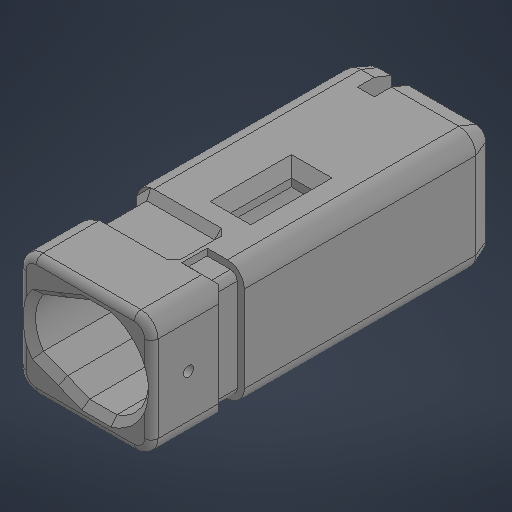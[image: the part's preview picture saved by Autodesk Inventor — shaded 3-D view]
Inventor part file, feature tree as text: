
AUTODESK INVENTOR PART (.ipt)
format: ipt  version: 2025.1 (Build 291241000, 241)  size: 1,372,672 bytes
history: native  units: in
note: dims shown in document units (in); Inventor stores cm internally (conversion verified against a paired STEP export)
features: extrude x9, sketch x8, chamfer x7, fillet x5, plane x1, projected_geometry x1
ambient origin geometry x8: Origin, YZ Plane, XZ Plane, XY Plane, X Axis, Y Axis, Z Axis, Center Point
bodies: Solid1 (feature_tree)
feature tree (31):
  extrude  "Extrusion1"  Depth=1.5354in
  extrude  "Extrusion2"  Depth=0.6988in
  chamfer  "Chamfer9"  Distance=3.9724in
  extrude  "Extrusion3"  Depth=3.9724in
  sketch  "Sketch5"  dims[d11=1.315in d12=1.0039in d13=0.5748in d14=0.2795in d15=0.2581in d16=0.1063in d17=0.5259in d18=0.4908in d30=3.9724in d31=-0.0019in]
  extrude  "Extrusion5"  Depth=0.0394in
  extrude  "Extrusion11"  TaperAngle=0.0deg  [1 undecoded]
  sketch  "Sketch9"  dims[d33=0.0394in d39=0.0394in]
  plane  "Work Plane1"
  extrude  "Extrusion9"  Depth=0.0394in
  chamfer  "Chamfer15"  Distance=0.7874in
  fillet  "Fillet3"  Radius=0.2953in
  chamfer  "Chamfer6"  Distance=0.0827in
  chamfer  "Chamfer11"  Distance=0.0787in
  fillet  "Fillet8"  Radius=0.2756in
  fillet  "Fillet12"  Radius=0.0787in
  extrude  "Extrusion14"  Depth=0.3937in
  chamfer  "Chamfer14"  Distance=0.6299in
  fillet  "Fillet14"  Radius=0.0787in
  fillet  "Fillet16"  Radius=0.0787in
  chamfer  "Chamfer17"  Distance=0.1969in
  extrude  "Extrusion16"  Depth=0.3937in TaperAngle=45.0deg
  chamfer  "Chamfer19"  Distance=0.0787in
  extrude  "Extrusion17"  Depth=0.3937in TaperAngle=0.0deg
  sketch  "Sketch1"  dims[d1=1.3976in d2=1.5354in]
  sketch  "Sketch2"  dims[d4=0.0in d5=0.6988in]
  sketch  "Sketch3"  dims[d6=0.7677in d7=3.9724in d8=0.0in]
  sketch  "Sketch12"  dims[d40=0.0787in d41=0.0in d42=0.0in]
  sketch  "Sketch14"  dims[d47=0.0in d48=0.0394in]
  sketch  "Sketch15"  dims[d49=0.0353in d56=0.7874in d57=0.2953in d60=0.0827in d61=0.0in d79=0.0787in d80=0.2756in d81=0.0787in d82=0.4724in d83=-1.3661in d84=0.6299in d85=0.0in d100=0.0787in d101=0.0787in d102=45.0deg d103=0.0787in d119=0.1969in d123=0.0787in d124=0.0787in d125=45.0deg d128=0.0787in d130=0.4331in d131=0.0in d137=0.6575in d143=0.0768in d144=0.0787in d145=45.0deg d146=0.0787in d156=0.2362in d157=0.3937in d158=0.0in d159=0.1181in d160=0.0787in d161=45.0deg d162=0.0787in d164=0.1102in d165=0.1181in d166=0.7087in d167=1.4961in d168=0.1181in d169=0.0787in d170=45.0deg d171=0.0394in d176=0.0787in d179=0.0787in d180=0.1969in d181=45.0deg d189=0.1969in d190=0.1969in d191=0.3543in d193=0.3937in d194=0.0in d195=0.1969in d196=0.0787in d197=45.0deg d198=0.3543in d199=0.1181in d200=0.3937in d201=0.0in d120=0.0in d121=0.0in d122=0.0in d126=0.0344in d127=0.0344in d129=0.0344in d182=0.0in]
  projected_geometry  "Projected Loop1"
note: 1 required parameter value undecoded (feature->parameter linkage not recoverable at this tier; creation-order binding heuristic only, values carry confidence <= 0.55)
